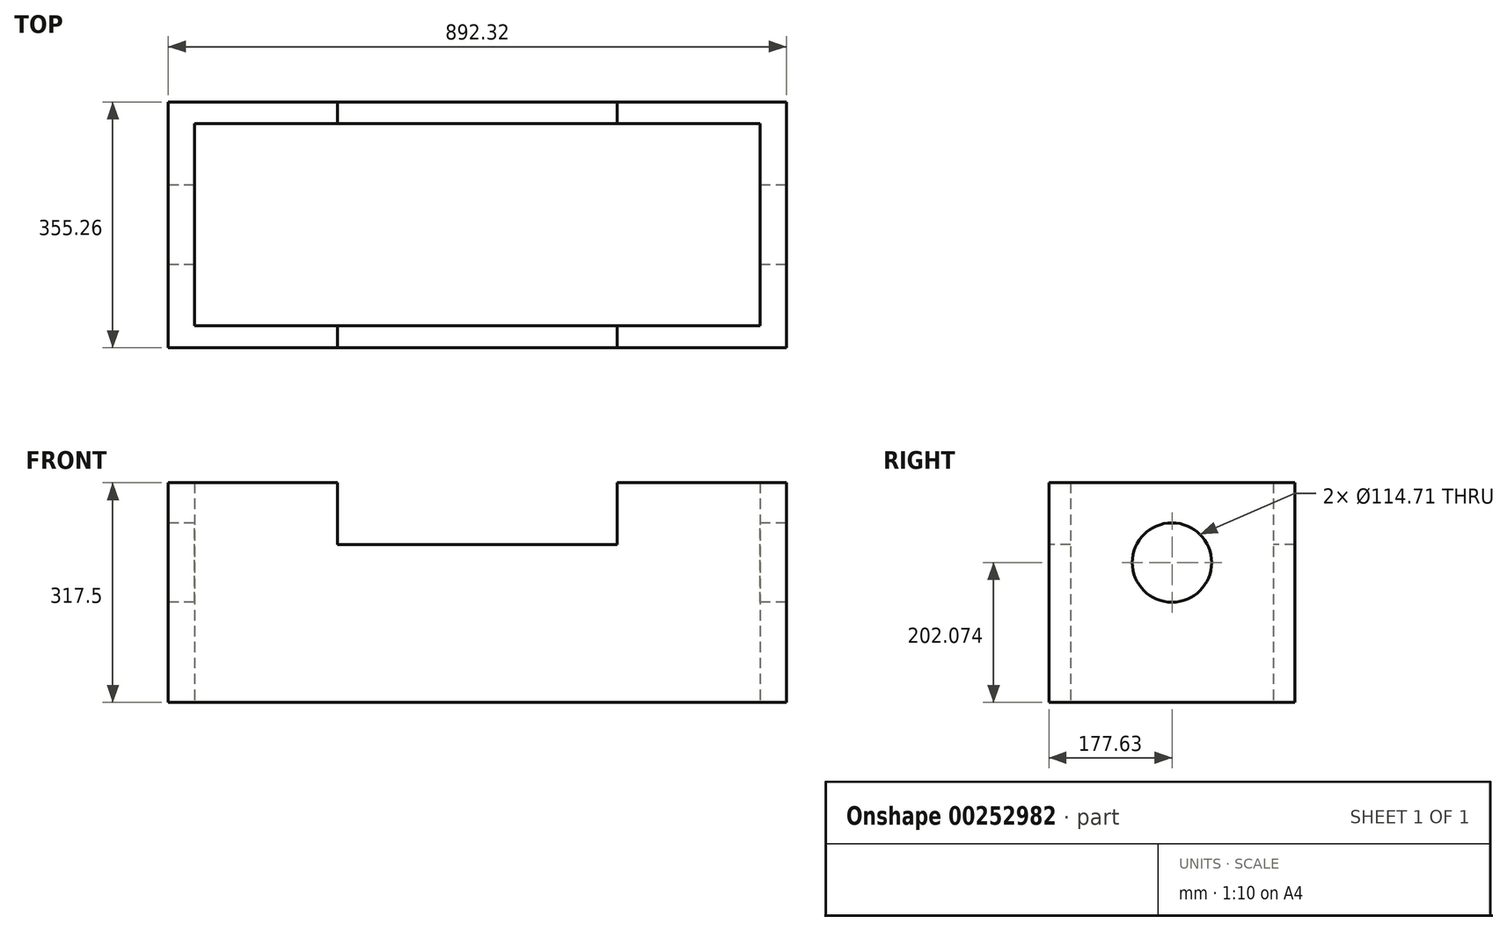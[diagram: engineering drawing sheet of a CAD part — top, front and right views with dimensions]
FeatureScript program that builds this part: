
annotation { "Feature Type Name" : "Feature", "Feature Type Description" : "" }
export const myFeature = defineFeature(function(context is Context, id is Id, definition is map)
    precondition{}
    {
        {
            var Q0;
            Q0=qCreatedBy(makeId("Top.planeOp"),FACE);
            var sketch = newSketch(context, id + "F0", { "sketchPlane" : qUnion([Q0])});
            skLineSegment(sketch, "E0.bottom", {"start": v(446.16, 177.63) * mm, "end": v(-446.16, 177.63) * mm});
            skLineSegment(sketch, "E0.top", {"start": v(446.16, -177.63) * mm, "end": v(-446.16, -177.63) * mm});
            skLineSegment(sketch, "E0.left", {"start": v(446.16, 177.63) * mm, "end": v(446.16, -177.63) * mm});
            skLineSegment(sketch, "E0.right", {"start": v(-446.16, 177.63) * mm, "end": v(-446.16, -177.63) * mm});
            skPoint(sketch, "E0.middle", {"position": v(0, 0) * mm});
            skLineSegment(sketch, "E1.bottom", {"start": v(408.33, 146.1) * mm, "end": v(-408.33, 146.1) * mm});
            skLineSegment(sketch, "E1.top", {"start": v(408.33, -146.1) * mm, "end": v(-408.33, -146.1) * mm});
            skLineSegment(sketch, "E1.left", {"start": v(408.33, 146.1) * mm, "end": v(408.33, -146.1) * mm});
            skLineSegment(sketch, "E1.right", {"start": v(-408.33, 146.1) * mm, "end": v(-408.33, -146.1) * mm});
            skSolve(sketch);
        }
        {
            var Q0;
            Q0=makeQuery(id+"F0.imprint","IMPRINT",FACE,{"disambiguationData":[TD([[makeQuery(id+"F0.imprint","IMPRINT",EDGE,{"derivedFrom":sQuery(id+"F0.wireOp",EDGE,"E0.bottom")}),1.0]])]});
            extrude(context, id + "F1", {"entities" : qUnion([Q0]), "depth" : 317.5 * mm});
        }
        {
            var Q0;
            Q0=makeQuery(id+"F1.opExtrude","SWEPT_FACE",FACE,{"disambiguationData":[OSD([sQuery(id+"F0.wireOp",EDGE,"E0.top")])]});
            var sketch = newSketch(context, id + "F2", { "sketchPlane" : qUnion([Q0])});
            skLineSegment(sketch, "E2.bottom", {"start": v(202.05, 406.8) * mm, "end": v(-202.05, 406.8) * mm});
            skLineSegment(sketch, "E2.top", {"start": v(202.05, 228.2) * mm, "end": v(-202.05, 228.2) * mm});
            skLineSegment(sketch, "E2.left", {"start": v(202.05, 406.8) * mm, "end": v(202.05, 228.2) * mm});
            skLineSegment(sketch, "E2.right", {"start": v(-202.05, 406.8) * mm, "end": v(-202.05, 228.2) * mm});
            skPoint(sketch, "E2.middle", {"position": v(0, 317.5) * mm});
            skSolve(sketch);
        }
        {
            var Q0;
            Q0=qSketchRegion(id+"F2",true);
            extrude(context, id + "F3", {"entities" : qUnion([Q0]), "operationType" : NewBodyOperationType.REMOVE, "endBound" : BoundingType.THROUGH_ALL, "oppositeDirection" : true, "depth" : 25.4 * mm});
        }
        {
            var Q0;
            Q0=makeQuery(id+"F1.opExtrude","SWEPT_FACE",FACE,{"disambiguationData":[OSD([sQuery(id+"F0.wireOp",EDGE,"E0.right")])]});
            var sketch = newSketch(context, id + "F4", { "sketchPlane" : qUnion([Q0])});
            skCircle(sketch, "E3", {"center": v(0, 202.07) * mm, "radius": 57.35 * mm});
            skSolve(sketch);
        }
        {
            var Q0;
            Q0=qSketchRegion(id+"F4",true);
            extrude(context, id + "F5", {"entities" : qUnion([Q0]), "operationType" : NewBodyOperationType.REMOVE, "endBound" : BoundingType.THROUGH_ALL, "oppositeDirection" : true, "depth" : 25.4 * mm});
        }
    });
